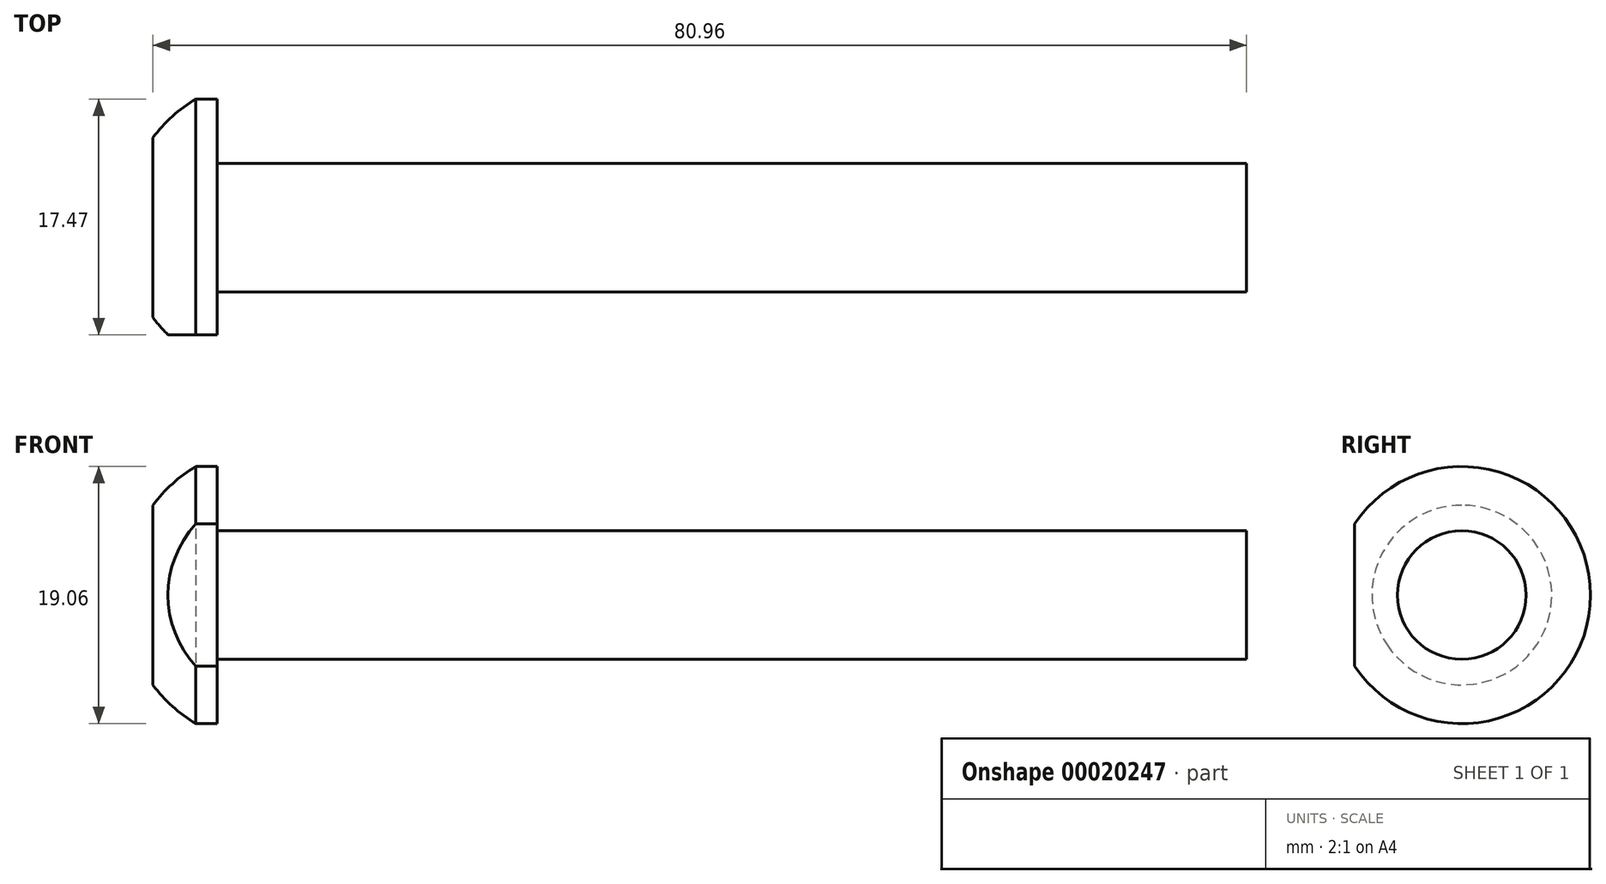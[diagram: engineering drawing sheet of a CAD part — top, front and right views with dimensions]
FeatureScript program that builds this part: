
annotation { "Feature Type Name" : "Feature", "Feature Type Description" : "" }
export const myFeature = defineFeature(function(context is Context, id is Id, definition is map)
    precondition{}
    {
        {
            var Q0;
            Q0=qCreatedBy(makeId("Top.planeOp"),FACE);
            var sketch = newSketch(context, id + "F0", { "sketchPlane" : qUnion([Q0])});
            skLineSegment(sketch, "E0", {"start": v(-16.43, 4.76) * mm, "end": v(59.77, 4.76) * mm});
            skLineSegment(sketch, "E1", {"start": v(59.77, 4.76) * mm, "end": v(59.77, 0) * mm});
            skLineSegment(sketch, "E2", {"start": v(59.77, 0) * mm, "end": v(-16.43, 0) * mm});
            skLineSegment(sketch, "E3", {"start": v(-16.43, 0) * mm, "end": v(-14.96, 0) * mm});
            skLineSegment(sketch, "E4", {"start": v(-16.43, 4.76) * mm, "end": v(-16.43, 0) * mm});
            skLineSegment(sketch, "E5", {"start": v(-16.43, 4.76) * mm, "end": v(-16.43, -4.76) * mm});
            skLineSegment(sketch, "E6", {"start": v(-16.43, -4.76) * mm, "end": v(-18.02, -4.76) * mm});
            skLineSegment(sketch, "E7", {"start": v(-18.02, -4.76) * mm, "end": v(-18.02, 4.76) * mm});
            skLineSegment(sketch, "E8", {"start": v(-18.02, 4.76) * mm, "end": v(-16.43, 4.76) * mm});
            skArc(sketch, "E9", {"start": v(-21.2, -1.9) * mm, "mid": v(-19.75, -3.48) * mm, "end": v(-18.02, -4.76) * mm});
            skLineSegment(sketch, "E10", {"start": v(-21.2, -1.9) * mm, "end": v(-21.2, 4.76) * mm});
            skLineSegment(sketch, "E11", {"start": v(-21.2, 4.76) * mm, "end": v(-18.02, 4.76) * mm});
            skSolve(sketch);
        }
        {
            var Q0;
            Q0 = qSketchRegion(id + "F0", true);
            var Q1;
            Q1=sQuery(id+"F0.wireOp",EDGE,"E0");
            revolve(context, id + "F1", {"entities" : qUnion([Q0]), "axis" : qUnion([Q1]), "revolveType" : RevolveType.FULL});
        }
        {
            var Q0;
            Q0=makeQuery(id+"F1.opRevolve","SWEPT_FACE",FACE,{"disambiguationData":[OSD([sQuery(id+"F0.wireOp",EDGE,"E10")])]});
            var sketch = newSketch(context, id + "F2", { "sketchPlane" : qUnion([Q0])});
            skLineSegment(sketch, "E12", {"start": v(0, 0) * mm, "end": v(-4.76, 0) * mm});
            skLineSegment(sketch, "E13", {"start": v(-4.76, 0) * mm, "end": v(3.18, 0) * mm});
            skLineSegment(sketch, "E14", {"start": v(3.18, 0) * mm, "end": v(3.18, 10.65) * mm});
            skLineSegment(sketch, "E15", {"start": v(3.18, 10.65) * mm, "end": v(11.2, 10.65) * mm});
            skLineSegment(sketch, "E16", {"start": v(11.2, 10.65) * mm, "end": v(11.2, 0) * mm});
            skLineSegment(sketch, "E17", {"start": v(11.2, 0) * mm, "end": v(3.18, 0) * mm});
            skLineSegment(sketch, "E18.MirrorCS", {"start": v(3.18, -10.65) * mm, "end": v(11.2, -10.65) * mm});
            skLineSegment(sketch, "E19.MirrorCS", {"start": v(11.2, -10.65) * mm, "end": v(11.2, 0) * mm});
            skLineSegment(sketch, "E20.MirrorCS", {"start": v(3.18, 0) * mm, "end": v(3.18, -10.65) * mm});
            skSolve(sketch);
        }
        {
            var Q0;
            Q0 = qSketchRegion(id + "F2", true);
            extrude(context, id + "F3", {"entities" : qUnion([Q0]), "operationType" : NewBodyOperationType.REMOVE, "oppositeDirection" : true, "depth" : 25.4 * mm});
        }
    });
